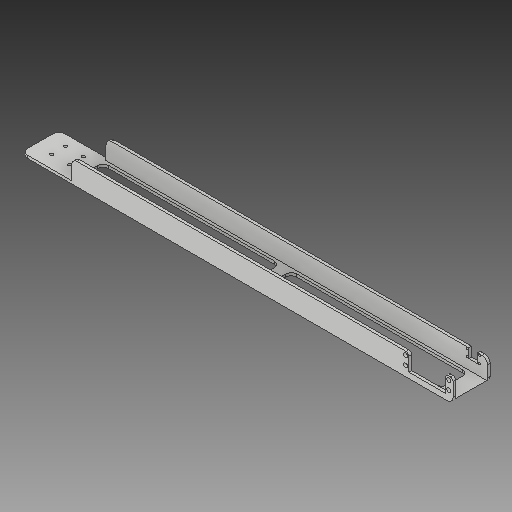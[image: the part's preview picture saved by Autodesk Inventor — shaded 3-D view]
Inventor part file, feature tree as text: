
AUTODESK INVENTOR PART (.ipt)
format: ipt  version: 2019 (Build 230136000, 136)  size: 280,064 bytes
history: native  units: in
note: dims shown in document units (in); Inventor stores cm internally (conversion verified against a paired STEP export)
features: sketch x6, extrude x5, projected_geometry x5, fillet x4, hole x1
ambient origin geometry x8: Origin, YZ Plane, XZ Plane, XY Plane, X Axis, Y Axis, Z Axis, Center Point
bodies: Solid1 (feature_tree)
feature tree (21):
  extrude  "Extrusion1"  Depth=1.685in
  extrude  "Extrusion2"  Depth=1.435in
  fillet  "Fillet1"  Radius=0.125in
  fillet  "Fillet2"  Radius=19.5in
  extrude  "Extrusion5"  Depth=1.0in
  fillet  "Fillet3"  Radius=0.75in
  extrude  "Extrusion6"  Depth=2.0in
  fillet  "Fillet4"  Radius=0.19in
  hole  "Hole1"  [1 undecoded]
  extrude  "Extrusion7"  Depth=0.25in
  sketch  "Sketch1"  dims[d0=1.0in d1=1.685in]
  sketch  "Sketch2"  dims[d2=0.875in d3=1.435in d4=0.125in d5=19.5in d6=0.0in]
  projected_geometry  "Projected Loop1"
  sketch  "Sketch6"  dims[d7=0.35in d8=1.0in d9=0.75in]
  projected_geometry  "Projected Loop4"
  sketch  "Sketch7"  dims[d10=2.0in d11=0.19in d12=0.19in]
  projected_geometry  "Projected Loop5"
  sketch  "Sketch8"  dims[d13=0.164in d14=0.3937in]
  projected_geometry  "Projected Loop6"
  sketch  "Sketch9"  dims[d15=0.19in d16=0.19in d19=0.5in d20=0.0in d26=0.197in d27=0.197in d28=1.9488in d29=1.9488in d30=0.3937in d43=0.125in d44=0.25in d46=2.25in d47=0.875in d48=5.0in d49=0.0in d50=0.25in d52=1.685in d53=0.25in d54=0.25in d55=2.25in d56=17.0in d57=8.0in d58=8.0in d59=0.25in d60=0.25in d61=0.5in d62=5.0in d63=0.0in d64=0.25in d70=0.8051in d71=0.6299in d72=0.4772in d73=0.7785in d74=0.1457in d75=0.75in d76=0.375in d77=0.25in d78=0.5635in d79=1.0in d80=0.8108in d97=0.097in d98=0.097in d99=0.097in d100=0.097in d101=0.376in d102=0.376in d103=0.546in d104=0.546in d105=0.936in d106=0.621in d107=0.621in d108=0.936in d109=0.3937in d110=0.423in d111=0.0761in d112=0.25in d113=0.0in]
  projected_geometry  "Projected Loop7"
note: 1 required parameter value undecoded (feature->parameter linkage not recoverable at this tier; creation-order binding heuristic only, values carry confidence <= 0.55)
